SOLIDWORKS PART (.sldprt)
format: sldprt  version: not decoded by parser v0  size: 129,536 bytes
history: native  units: mm
features: sketch x4, cut_extrude x3, material x1, extrude x1, fillet x1 (+13 scaffold rows collapsed)
feature tree (23):
  scaffold x13  (default folders/planes/origin — collapsed)
  material  "Material <not specified>"
  sketch  "Sketch1"  dims[c1.D1=16.0mm c1.D2=16.0mm c2.D1=7.0mm c2.D3=3.0mm c2.D2=60.0mm]
  extrude  "Boss-Extrude1"  Depth=5mm
  sketch  "Sketch2"  dims[D1=2.0mm]
  cut_extrude  "Cut-Extrude1"  Depth=5mm
  sketch  "Sketch3"  dims[c1.D2=2.459mm c1.D1=3.0mm c2.D2=55.0mm c2.D3=3.0mm]
  cut_extrude  "Cut-Extrude2"  Depth=5mm
  fillet  "Fillet1"  Radius=1mm
  sketch  "Sketch4"  dims[D1=2.9mm]
  cut_extrude  "Cut-Extrude3"  Depth=5mm
decode coverage: 9 of 9 modeling features carry decoded parameters
note: suppression state not decoded; provenance and decode notes live in map.json
